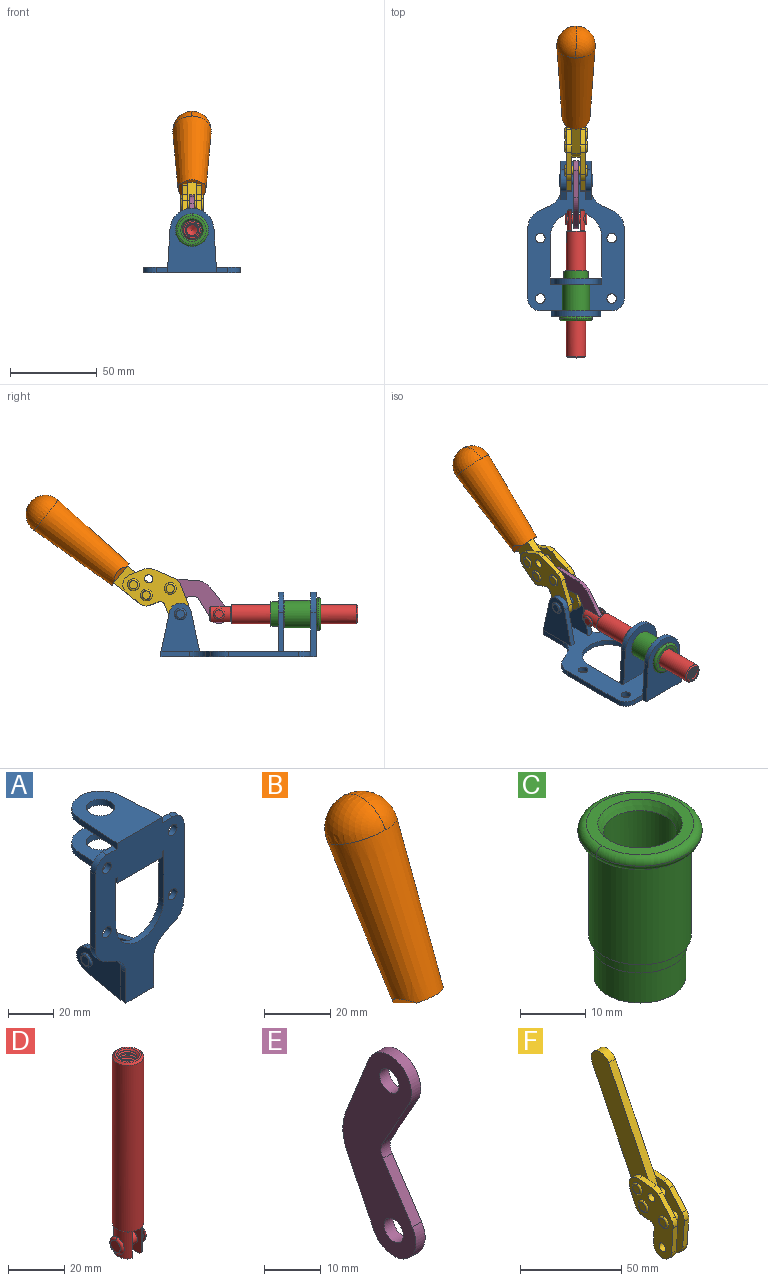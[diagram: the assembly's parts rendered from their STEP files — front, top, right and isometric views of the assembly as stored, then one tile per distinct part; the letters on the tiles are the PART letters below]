
ASSEMBLY  parts=6 mates=6
PART A: 55 faces, bbox 55.7x37.4x89.8 mm
  f0: torus R=2.41mm, axis (-1,0,0), area 15mm2, adj f11,f15,f25
  f1: torus R=2.41mm, axis (-1,0,0), area 15mm2, adj f10,f12,f22
  f2: cylinder r=2.78mm len=5.56mm, axis (0,-1,0), area 54.2mm2, adj f30,f54
  f3: cylinder r=14.99mm len=29.97mm, axis (0,-1,0), area 145.9mm2, adj f30,f49,f53,f54
  f4: cylinder r=2.78mm len=5.56mm, axis (0,-1,0), area 54.2mm2, adj f30,f54
  f5: cylinder r=2.78mm len=5.56mm, axis (0,-1,0), area 54.2mm2, adj f30,f54
  f6: cylinder r=2.78mm len=5.56mm, axis (0,-1,0), area 54.2mm2, adj f30,f54
  f7: cylinder r=6.35mm len=12.7mm, axis (0,0,1), area 123.6mm2, adj f27,f51
  f8: cylinder r=6.35mm len=12.7mm, axis (0,0,-1), area 124.7mm2, adj f21,f35
  f9: cylinder r=2.41mm len=11.18mm, axis (-1,0,0), area 169.4mm2, adj f16,f19
  f10: plane 4.83x4.83mm, normal (1,0,0), area 18.3mm2, adj f1,f12
  f11: plane 4.83x4.83mm, normal (-1,0,0), area 18.3mm2, adj f0,f15
  f12: torus R=2.41mm, axis (-1,0,0), area 15mm2, adj f1,f10,f22
  f13: cylinder r=6.35mm len=12.41mm, axis (1,0,0), area 53.4mm2, adj f18,f19,f22,f23
  f14: cylinder r=6.35mm len=12.41mm, axis (-1,0,0), area 53.4mm2, adj f16,f17,f24,f25
  f15: torus R=2.41mm, axis (-1,0,0), area 15mm2, adj f0,f11,f25
  f16: plane 27.86x22.35mm, normal (1,0,0), area 425.4mm2, adj f9,f14,f17,f24,f30
  f17: plane 22.86x4.97mm, normal (0,0.21,0.98), area 72.5mm2, adj f14,f16,f25,f30
  f18: plane 22.86x4.97mm, normal (0,0.21,0.98), area 72.5mm2, adj f13,f19,f22,f30
  f19: plane 27.86x22.35mm, normal (-1,0,0), area 425.4mm2, adj f9,f13,f18,f23,f30
  f20: cylinder r=12.7mm len=25.35mm, axis (0,0,-1), area 119.8mm2, adj f21,f34,f35,f36
  f21: plane 34.21x28.07mm, normal (0,0,-1), area 702.4mm2, adj f8,f20,f30,f34,f36
  f22: plane 27.96x22.45mm, normal (1,0,0), area 407.2mm2, adj f1,f12,f13,f18,f23,f30,f42,f43
  f23: plane 22.86x4.97mm, normal (0,0.21,-0.98), area 72.5mm2, adj f13,f19,f22,f44
  f24: plane 22.86x4.97mm, normal (0,0.21,-0.98), area 72.5mm2, adj f14,f16,f25,f44
  f25: plane 27.86x22.35mm, normal (-1,0,0), area 407.1mm2, adj f0,f14,f15,f17,f24,f30,f45,f46
  f26: plane 3.1x0.95mm, normal (0,0,-1), area 2.7mm2, adj f30,f49,f50,f54
  f27: plane 34.21x28.07mm, normal (0,0,1), area 702.4mm2, adj f7,f28,f30,f50,f52
  f28: cylinder r=12.7mm len=25.35mm, axis (0,0,1), area 118.8mm2, adj f27,f50,f51,f52
  f29: plane 3.1x0.95mm, normal (0,0,-1), area 2.7mm2, adj f30,f52,f53,f54
  f30: plane 86.54x55.63mm, normal (0,1,0), area 2362.9mm2, adj f2,f3,f4,f5,f6,f16,f17,f18
  f31: plane 40.56x3.1mm, normal (-1,0,0), area 125.7mm2, adj f30,f32,f48,f54
  f32: cylinder r=7.11mm len=7.11mm, axis (0,-1,0), area 34.6mm2, adj f30,f31,f33,f54
  f33: plane 6.67x3.1mm, normal (0,0,1), area 20.4mm2, adj f30,f32,f34,f54
  f34: plane 25.39x3.13mm, normal (-1,0.06,0), area 79.5mm2, adj f20,f21,f33,f35,f54
  f35: plane 37.31x28.45mm, normal (0,0,1), area 789.9mm2, adj f8,f20,f34,f36,f54
  f36: plane 25.39x3.13mm, normal (1,0.06,0), area 79.5mm2, adj f20,f21,f35,f37,f54
  f37: plane 6.67x3.1mm, normal (0,0,1), area 20.4mm2, adj f30,f36,f38,f54
  f38: cylinder r=7.11mm len=7.11mm, axis (0,-1,0), area 34.6mm2, adj f30,f37,f39,f54
  f39: plane 40.56x3.1mm, normal (1,0,0), area 125.7mm2, adj f30,f38,f40,f54
  f40: cylinder r=11.18mm len=10.16mm, axis (0,-1,0), area 39.5mm2, adj f30,f39,f41,f54
  f41: plane 6.09x3.1mm, normal (0.42,0,-0.91), area 20.8mm2, adj f30,f40,f42,f54
  f42: cylinder r=11.18mm len=9.41mm, axis (0,-1,0), area 37.2mm2, adj f22,f30,f41,f43,f54
  f43: plane 16.5x3.1mm, normal (1,0,0), area 51.1mm2, adj f22,f42,f44,f54
  f44: plane 17.37x3.1mm, normal (0,0,-1), area 53.8mm2, adj f23,f24,f30,f43,f45,f54
  f45: plane 16.5x3.1mm, normal (-1,0,0), area 51.1mm2, adj f25,f44,f46,f54
  f46: cylinder r=11.18mm len=9.41mm, axis (0,-1,0), area 37.2mm2, adj f25,f30,f45,f47,f54
  f47: plane 6.09x3.1mm, normal (-0.42,0,-0.91), area 20.8mm2, adj f30,f46,f48,f54
  f48: cylinder r=11.18mm len=10.16mm, axis (0,-1,0), area 39.5mm2, adj f30,f31,f47,f54
  f49: plane 26.54x3.1mm, normal (-1,0,0), area 82.3mm2, adj f3,f26,f30,f54
  f50: plane 25.39x3.1mm, normal (1,0.06,0), area 78.8mm2, adj f26,f27,f28,f51,f54
  f51: plane 37.31x28.45mm, normal (0,0,-1), area 789.9mm2, adj f7,f28,f50,f52,f54
  f52: plane 25.39x3.1mm, normal (-1,0.06,0), area 78.8mm2, adj f27,f28,f29,f51,f54
  f53: plane 26.54x3.1mm, normal (1,0,0), area 82.3mm2, adj f3,f29,f30,f54
  f54: plane 89.66x55.63mm, normal (0,-1,0), area 2678.5mm2, adj f2,f3,f4,f5,f6,f26,f29,f31
PART B: 11 faces, bbox 22.3x42.6x64.5 mm
  f0: sphere r=11.13mm, area 411.4mm2, adj f1,f8
  f1: cone r=11.11mm half-angle=3.3deg, axis (0,0.44,0.9), area 3251.8mm2, adj f0,f7,f8,f9,f10
  f2: cylinder r=6.16mm len=11.7mm, axis (1,0,0), area 89.5mm2, adj f3,f4,f5,f6
  f3: plane 60.23x36.75mm, normal (-1,0,0), area 763.6mm2, adj f2,f4,f6,f10
  f4: plane 51.37x25.05mm, normal (0,0.9,-0.44), area 264.2mm2, adj f2,f3,f5,f10
  f5: plane 60.23x36.75mm, normal (1,0,0), area 763.6mm2, adj f2,f4,f6,f10
  f6: plane 51.37x25.05mm, normal (0,-0.9,0.44), area 264.2mm2, adj f2,f3,f5,f10
  f7: plane 9.95x5.95mm, normal (0.71,-0.31,-0.64), area 25.8mm2, adj f1,f10
  f8: sphere r=11.13mm, area 411.4mm2, adj f0,f1
  f9: plane 9.95x5.95mm, normal (-0.71,-0.31,-0.64), area 25.8mm2, adj f1,f10
  f10: plane 14.27x11.38mm, normal (0,-0.44,-0.9), area 106.7mm2, adj f1,f3,f4,f5,f6,f7,f9
PART C: 15 faces, bbox 20.6x20.6x28.7 mm
  f0: torus R=8.26mm, axis (0,0,1), area 56.8mm2, adj f1,f10,f12
  f1: torus R=8.26mm, axis (0,0,1), area 56.8mm2, adj f0,f6,f13
  f2: cylinder r=5.59mm len=25.91mm, axis (0,0,1), area 909.6mm2, adj f3,f4
  f3: cone r=6.86mm half-angle=45deg, axis (0,0,-1), area 70.2mm2, adj f2,f14
  f4: cone r=6.47mm half-angle=30deg, axis (0,0,1), area 66.7mm2, adj f2,f13
  f5: cylinder r=7.04mm len=14.07mm, axis (0,0,1), area 252.6mm2, adj f11,f14
  f6: torus R=8.26mm, axis (0,0,1), area 56.8mm2, adj f1,f12,f13
  f7: cylinder r=7.16mm len=14.33mm, axis (0,0,1), area 91.5mm2, adj f9,f11
  f8: cylinder r=7.86mm len=18.42mm, axis (0,0,1), area 909.6mm2, adj f9,f10
  f9: plane 15.72x15.72mm, normal (0,0,-1), area 33mm2, adj f7,f8
  f10: plane 16.51x16.51mm, normal (0,0,-1), area 19.9mm2, adj f0,f8,f12
  f11: plane 14.33x14.33mm, normal (0,0,-1), area 5.7mm2, adj f5,f7
  f12: torus R=8.26mm, axis (0,0,1), area 56.8mm2, adj f0,f6,f10
  f13: plane 16.51x16.51mm, normal (0,0,1), area 82.7mm2, adj f1,f4,f6
  f14: plane 14.07x14.07mm, normal (0,0,-1), area 7.8mm2, adj f3,f5
PART D: 48 faces, bbox 12.6x11.1x86.1 mm
  f0: torus R=2.41mm, axis (-1,0,0), area 15mm2, adj f30,f32,f34
  f1: torus R=2.41mm, axis (-1,0,0), area 15mm2, adj f29,f31,f33
  f2: cylinder r=5.54mm len=72.39mm, axis (0,0,1), area 2518.5mm2, adj f3,f4,f42,f43
  f3: cone r=5.54mm half-angle=45deg, axis (0,0,1), area 7.6mm2, adj f2,f5,f41
  f4: cone r=5.54mm half-angle=45deg, axis (0,0,-1), area 34.9mm2, adj f2,f39
  f5: cylinder r=5.08mm len=11.48mm, axis (0,0,1), area 108.3mm2, adj f3,f7,f8,f41
  f6: cylinder r=2.41mm len=4.83mm, axis (-1,0,0), area 71.2mm2, adj f40,f41
  f7: cylinder r=2.41mm len=4.83mm, axis (-1,0,0), area 7.6mm2, adj f5,f34
  f8: cone r=5.08mm half-angle=45deg, axis (0,0,1), area 10.6mm2, adj f5,f37,f41
  f9: cone r=3.98mm half-angle=45deg, axis (0,0,1), area 17.6mm2, adj f27,f39,f45,f46,f47
  f10: cylinder r=2.41mm len=4.83mm, axis (-1,0,0), area 7.6mm2, adj f33,f38
  f11: cylinder r=3.2mm len=6.4mm, axis (0,0,1), area 78.4mm2, adj f12,f28,f44,f45,f47
  f12: cylinder r=3.2mm len=6.4mm, axis (0,0,1), area 10.5mm2, adj f11,f13,f45,f47
  f13: cylinder r=3.2mm len=6.4mm, axis (0,0,1), area 10.5mm2, adj f12,f14,f45,f47
  f14: cylinder r=3.2mm len=6.4mm, axis (0,0,1), area 10.5mm2, adj f13,f15,f45,f47
  f15: cylinder r=3.2mm len=6.4mm, axis (0,0,1), area 10.5mm2, adj f14,f16,f45,f47
  f16: cylinder r=3.2mm len=6.4mm, axis (0,0,1), area 10.5mm2, adj f15,f17,f45,f47
  f17: cylinder r=3.2mm len=6.4mm, axis (0,0,1), area 10.5mm2, adj f16,f18,f45,f47
  f18: cylinder r=3.2mm len=6.4mm, axis (0,0,1), area 10.5mm2, adj f17,f19,f45,f47
  f19: cylinder r=3.2mm len=6.4mm, axis (0,0,1), area 10.5mm2, adj f18,f20,f45,f47
  f20: cylinder r=3.2mm len=6.4mm, axis (0,0,1), area 10.5mm2, adj f19,f21,f45,f47
  f21: cylinder r=3.2mm len=6.4mm, axis (0,0,1), area 10.5mm2, adj f20,f22,f45,f47
  f22: cylinder r=3.2mm len=6.4mm, axis (0,0,1), area 10.5mm2, adj f21,f23,f45,f47
  f23: cylinder r=3.2mm len=6.4mm, axis (0,0,1), area 10.5mm2, adj f22,f24,f45,f47
  f24: cylinder r=3.2mm len=6.4mm, axis (0,0,1), area 10.5mm2, adj f23,f25,f45,f47
  f25: cylinder r=3.2mm len=6.4mm, axis (0,0,1), area 10.5mm2, adj f24,f26,f45,f47
  f26: cylinder r=3.2mm len=6.4mm, axis (0,0,1), area 10.5mm2, adj f25,f27,f45,f47
  f27: cylinder r=3.2mm len=6.4mm, axis (0,0,1), area 7.4mm2, adj f9,f26,f45,f47
  f28: cone r=3.2mm half-angle=60deg, axis (0,0,1), area 37.2mm2, adj f11
  f29: plane 4.83x4.83mm, normal (-1,0,0), area 18.3mm2, adj f1,f31
  f30: plane 4.83x4.83mm, normal (1,0,0), area 18.3mm2, adj f0,f32
  f31: torus R=2.41mm, axis (-1,0,0), area 15mm2, adj f1,f29,f33
  f32: torus R=2.41mm, axis (-1,0,0), area 15mm2, adj f0,f30,f34
  f33: plane 6.83x6.83mm, normal (1,0,0), area 18.3mm2, adj f1,f10,f31
  f34: plane 6.83x6.83mm, normal (-1,0,0), area 18.3mm2, adj f0,f7,f32
  f35: cone r=5.08mm half-angle=45deg, axis (0,0,1), area 10.6mm2, adj f36,f38,f40
  f36: plane 7.25x1.97mm, normal (0,0,-1), area 10mm2, adj f35,f40
  f37: plane 7.25x1.97mm, normal (0,0,-1), area 10mm2, adj f8,f41
  f38: cylinder r=5.08mm len=11.48mm, axis (0,0,1), area 108.3mm2, adj f10,f35,f40,f42
  f39: plane 9.55x9.55mm, normal (0,0,1), area 22mm2, adj f4,f9
  f40: plane 12.76x10.09mm, normal (1,0,0), area 95.7mm2, adj f6,f35,f36,f38,f42,f43
  f41: plane 12.76x10.09mm, normal (-1,0,0), area 95.7mm2, adj f3,f5,f6,f8,f37,f43
  f42: cone r=5.54mm half-angle=45deg, axis (0,0,1), area 7.6mm2, adj f2,f38,f40
  f43: plane 11.07x4.7mm, normal (0,0,-1), area 50.4mm2, adj f2,f40,f41
  f44: plane 0.89x0.62mm, normal (-1,0,0), area 0.3mm2, adj f11,f45,f46,f47
  f45: bspline ~24.8x7.63mm, area 266.6mm2, adj f9,f11,f12,f13,f14,f15,f16,f17
  f46: bspline ~24.87x7.63mm, area 73.6mm2, adj f9,f44,f45,f47
  f47: bspline ~24.98x7.63mm, area 272.5mm2, adj f9,f11,f12,f13,f14,f15,f16,f17
PART E: 12 faces, bbox 2.3x18.2x42.8 mm
  f0: cylinder r=2.4mm len=4.8mm, axis (1,0,0), area 34.9mm2, adj f4,f11
  f1: cylinder r=10.41mm len=8.47mm, axis (1,0,0), area 20.2mm2, adj f4,f9,f10,f11
  f2: cylinder r=3.05mm len=3.16mm, axis (1,0,0), area 7.7mm2, adj f4,f6,f7,f11
  f3: cylinder r=2.4mm len=4.8mm, axis (1,0,0), area 34.9mm2, adj f4,f11
  f4: plane 42.81x18.23mm, normal (-1,0,0), area 414.1mm2, adj f0,f1,f2,f3,f5,f6,f7,f8
  f5: cylinder r=5.54mm len=10.67mm, axis (1,0,0), area 41.8mm2, adj f4,f6,f10,f11
  f6: plane 11.66x6.53mm, normal (0,-0.87,-0.49), area 30.9mm2, adj f2,f4,f5,f11
  f7: plane 11.17x7.33mm, normal (0,-0.84,0.55), area 30.9mm2, adj f2,f4,f8,f11
  f8: cylinder r=5.54mm len=10.51mm, axis (1,0,0), area 41.8mm2, adj f4,f7,f9,f11
  f9: plane 13.67x6.67mm, normal (0,0.9,-0.44), area 35.1mm2, adj f1,f4,f8,f11
  f10: plane 14.1x5.7mm, normal (0,0.93,0.37), area 35.1mm2, adj f1,f4,f5,f11
  f11: plane 42.81x18.23mm, normal (1,0,0), area 414.1mm2, adj f0,f1,f2,f3,f5,f6,f7,f8
PART F: 59 faces, bbox 12.9x60.2x99.6 mm
  f0: torus R=2.39mm, axis (-1,0,0), area 14.9mm2, adj f20,f43,f51
  f1: torus R=2.39mm, axis (-1,0,0), area 14.9mm2, adj f19,f42,f51
  f2: torus R=2.39mm, axis (-1,0,0), area 14.9mm2, adj f18,f35,f51
  f3: torus R=2.39mm, axis (-1,0,0), area 14.9mm2, adj f14,f17,f23
  f4: torus R=2.39mm, axis (-1,0,0), area 14.9mm2, adj f13,f16,f23
  f5: torus R=2.39mm, axis (-1,0,0), area 14.9mm2, adj f12,f15,f23
  f6: cylinder r=2.39mm len=4.78mm, axis (1,0,0), area 46.5mm2, adj f48,f50,f51
  f7: cylinder r=2.39mm len=4.78mm, axis (1,0,0), area 46.5mm2, adj f50,f51
  f8: cylinder r=6.35mm len=12.68mm, axis (1,0,0), area 61.8mm2, adj f38,f39,f50,f51
  f9: cylinder r=2.39mm len=4.78mm, axis (-1,0,0), area 70.5mm2, adj f46,f50
  f10: cylinder r=2.39mm len=4.78mm, axis (-1,0,0), area 46.5mm2, adj f23,f45,f46
  f11: cylinder r=2.39mm len=4.78mm, axis (-1,0,0), area 46.5mm2, adj f23,f46
  f12: plane 4.78x4.78mm, normal (1,0,0), area 17.9mm2, adj f5,f15
  f13: plane 4.78x4.78mm, normal (1,0,0), area 17.9mm2, adj f4,f16
  f14: plane 4.78x4.78mm, normal (1,0,0), area 17.9mm2, adj f3,f17
  f15: torus R=2.39mm, axis (-1,0,0), area 14.9mm2, adj f5,f12,f23
  f16: torus R=2.39mm, axis (-1,0,0), area 14.9mm2, adj f4,f13,f23
  f17: torus R=2.39mm, axis (-1,0,0), area 14.9mm2, adj f3,f14,f23
  f18: plane 4.78x4.78mm, normal (-1,0,0), area 17.9mm2, adj f2,f35
  f19: plane 4.78x4.78mm, normal (-1,0,0), area 17.9mm2, adj f1,f42
  f20: plane 4.78x4.78mm, normal (-1,0,0), area 17.9mm2, adj f0,f43
  f21: plane 2.26x0.2mm, normal (1,0,0), area 0.2mm2, adj f31,f44
  f22: plane 2.26x0.2mm, normal (-1,0,0), area 0.2mm2, adj f41,f44
  f23: plane 39.37x30.77mm, normal (1,0,0), area 565.5mm2, adj f3,f4,f5,f10,f11,f15,f16,f17
  f24: cylinder r=6.1mm len=4.15mm, axis (-1,0,0), area 14.7mm2, adj f23,f25,f32,f46
  f25: plane 10.25x9.01mm, normal (0,-0.75,0.66), area 42.3mm2, adj f23,f24,f26,f46
  f26: cylinder r=6.35mm len=4.64mm, axis (-1,0,0), area 15.6mm2, adj f23,f25,f27,f46
  f27: plane 15.84x3.1mm, normal (0,-1,-0.07), area 49.2mm2, adj f23,f26,f28,f46
  f28: cylinder r=6.35mm len=12.68mm, axis (-1,0,0), area 61.8mm2, adj f23,f27,f29,f46
  f29: plane 8.11x3.1mm, normal (0,1,0.07), area 25.2mm2, adj f23,f28,f30,f46
  f30: cylinder r=3.05mm len=3.25mm, axis (-1,0,0), area 14.8mm2, adj f23,f29,f31,f46
  f31: plane 5.99x3.1mm, normal (0,0.07,-1), area 18.6mm2, adj f21,f23,f30,f44,f46
  f32: plane 9.5x3.1mm, normal (0,-0.07,1), area 29.5mm2, adj f23,f24,f33,f46,f47
  f33: cylinder r=6.1mm len=8.63mm, axis (-1,0,0), area 39.1mm2, adj f23,f32,f34,f47
  f34: plane 8.65x3.96mm, normal (0,0.91,-0.42), area 29.5mm2, adj f23,f33,f44,f47
  f35: torus R=2.39mm, axis (-1,0,0), area 14.9mm2, adj f2,f18,f51
  f36: plane 10.25x9.01mm, normal (0,-0.75,0.66), area 42.3mm2, adj f37,f49,f50,f51
  f37: cylinder r=6.35mm len=4.64mm, axis (1,0,0), area 15.6mm2, adj f36,f38,f50,f51
  f38: plane 15.84x3.1mm, normal (0,-1,-0.07), area 49.2mm2, adj f8,f37,f50,f51
  f39: plane 8.11x3.1mm, normal (0,1,0.07), area 25.2mm2, adj f8,f40,f50,f51
  f40: cylinder r=3.05mm len=3.25mm, axis (1,0,0), area 14.8mm2, adj f39,f41,f50,f51
  f41: plane 5.99x3.1mm, normal (0,0.07,-1), area 18.6mm2, adj f22,f40,f44,f50,f51
  f42: torus R=2.39mm, axis (-1,0,0), area 14.9mm2, adj f1,f19,f51
  f43: torus R=2.39mm, axis (-1,0,0), area 14.9mm2, adj f0,f20,f51
  f44: cylinder r=6.35mm len=12.12mm, axis (-1,0,0), area 128.9mm2, adj f21,f22,f23,f31,f34,f41,f46,f47
  f45: plane 2.65x1.35mm, normal (1,0,0), area 1mm2, adj f10,f55
  f46: plane 39.08x20.42mm, normal (-1,0,0), area 412.5mm2, adj f9,f10,f11,f24,f25,f26,f27,f28
  f47: plane 77.62x39.82mm, normal (1,0,0), area 850mm2, adj f32,f33,f34,f44,f53,f54,f55
  f48: plane 2.65x1.35mm, normal (-1,0,0), area 1mm2, adj f6,f55
  f49: cylinder r=6.1mm len=4.15mm, axis (1,0,0), area 14.7mm2, adj f36,f50,f51,f56
  f50: plane 39.08x20.42mm, normal (1,0,0), area 412.5mm2, adj f6,f7,f8,f9,f36,f37,f38,f39
  f51: plane 39.37x30.77mm, normal (-1,0,0), area 565.5mm2, adj f0,f1,f2,f6,f7,f8,f35,f36
  f52: plane 8.65x3.96mm, normal (0,0.91,-0.42), area 29.5mm2, adj f44,f51,f57,f58
  f53: plane 68.49x33.4mm, normal (0,0.9,-0.44), area 358.1mm2, adj f44,f47,f54,f58
  f54: cylinder r=6.35mm len=12.06mm, axis (1,0,0), area 93.7mm2, adj f47,f53,f55,f58
  f55: plane 68.49x33.4mm, normal (0,-0.9,0.44), area 358.1mm2, adj f44,f45,f46,f47,f48,f50,f54,f58
  f56: plane 9.5x3.1mm, normal (0,-0.07,1), area 29.5mm2, adj f49,f50,f51,f57,f58
  f57: cylinder r=6.1mm len=8.63mm, axis (1,0,0), area 39.1mm2, adj f51,f52,f56,f58
  f58: plane 77.62x39.82mm, normal (-1,0,0), area 850mm2, adj f44,f52,f53,f54,f55,f56,f57
PLACE A rot(axis=(1,0,0),90deg) t=(-0.46,7.95,0.11)mm fixed
PLACE B rot(axis=(-1,0,0),25.4deg) t=(-0.46,31.6,64.28)mm
PLACE C rot(axis=(0.58,-0.58,0.58),120deg) t=(24.16,7.95,24.72)mm
PLACE D rot(axis=(1,0,0),90deg) t=(-0.46,33.21,0.11)mm
PLACE E rot(axis=(1,0,0),119.7deg) t=(-0.46,43.38,11.03)mm
PLACE F rot(axis=(-1,0,0),25.4deg) t=(-0.46,31.6,64.28)mm
MATE revolute D.f6 <-> E.f5  axis (-1,0,0) through (-0.46,17.74,24.72)mm
MATE fastened C.f2 <-> A.f7  axis (0,-1,0) through (-0.46,-38.45,24.72)mm
MATE slider A.f7 <-> D.f2  axis (0,-1,0) through (-0.46,-38.45,24.72)mm
MATE revolute F.f7 <-> A.f0  axis (-1,0,0) through (-0.46,40.04,24.72)mm
MATE revolute F.f4 <-> E.f3  axis (-1,0,0) through (-0.46,45.84,39.5)mm
MATE fastened F.f54 <-> B.f2  axis (1,0,0) through (-0.46,119.28,83.22)mm
